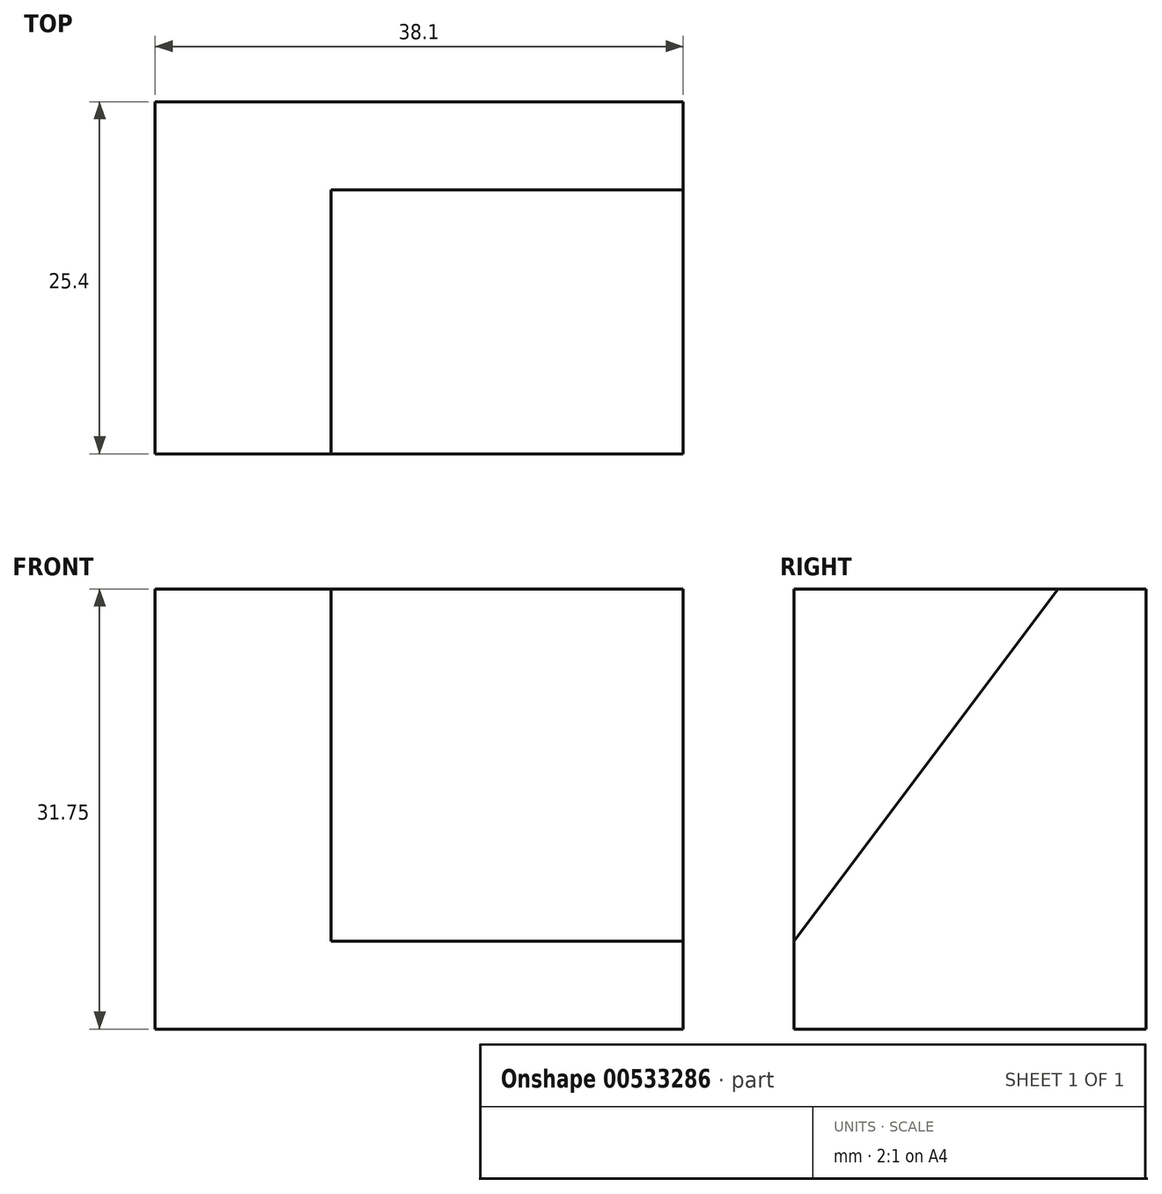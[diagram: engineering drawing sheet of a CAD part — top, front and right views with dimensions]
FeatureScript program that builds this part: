
annotation { "Feature Type Name" : "Feature", "Feature Type Description" : "" }
export const myFeature = defineFeature(function(context is Context, id is Id, definition is map)
    precondition{}
    {
        {
            var Q0;
            Q0=qCreatedBy(makeId("Front.planeOp"),FACE);
            var sketch = newSketch(context, id + "F0", { "sketchPlane" : qUnion([Q0])});
            skLineSegment(sketch, "E0", {"start": v(-59.7, 0) * mm, "end": v(-21.6, 0) * mm});
            skLineSegment(sketch, "E1", {"start": v(-59.7, 0) * mm, "end": v(-59.7, 31.75) * mm});
            skLineSegment(sketch, "E2", {"start": v(-21.6, 0) * mm, "end": v(-21.6, 31.75) * mm});
            skLineSegment(sketch, "E3", {"start": v(-21.6, 31.75) * mm, "end": v(-59.7, 31.75) * mm});
            skSolve(sketch);
        }
        {
            var Q0;
            Q0=makeQuery(id+"F0.imprint","IMPRINT",FACE,{"disambiguationData":[TD([[makeQuery(id+"F0.imprint","IMPRINT",EDGE,{"derivedFrom":sQuery(id+"F0.wireOp",EDGE,"E0")}),1.0]])]});
            extrude(context, id + "F1", {"entities" : qUnion([Q0]), "depth" : 25.4 * mm, "offsetDistance" : 25.4 * mm});
        }
        {
            var Q0;
            Q0=makeQuery(id+"F1.opExtrude","CAP_FACE",FACE,{"disambiguationData":[OSD([sQuery(id+"F0.wireOp",EDGE,"E0"),sQuery(id+"F0.wireOp",EDGE,"E1"),sQuery(id+"F0.wireOp",EDGE,"E2"),sQuery(id+"F0.wireOp",EDGE,"E3")])],"isStart":false});
            var sketch = newSketch(context, id + "F2", { "sketchPlane" : qUnion([Q0])});
            skSolve(sketch);
        }
        {
            var Q0;
            Q0=makeQuery(id+"F2.imprint","IMPRINT",FACE,{"disambiguationData":[TD([[makeQuery(id+"F2.imprint","IMPRINT",EDGE,{"derivedFrom":makeQuery(id+"F1.opExtrude","CAP_EDGE",EDGE,{"disambiguationData":[OSD([sQuery(id+"F0.wireOp",EDGE,"E0")])],"isStart":false})}),1.0]])]});
            extrude(context, id + "F3", {"entities" : qUnion([Q0]), "operationType" : NewBodyOperationType.REMOVE, "depth" : 25.4 * mm, "offsetDistance" : 25.4 * mm});
        }
        {
            var Q0;
            Q0=makeQuery(id+"F1.opExtrude","SWEPT_FACE",FACE,{"disambiguationData":[OSD([sQuery(id+"F0.wireOp",EDGE,"E2")])]});
            var sketch = newSketch(context, id + "F4", { "sketchPlane" : qUnion([Q0])});
            skLineSegment(sketch, "E4", {"start": v(-6.35, 31.75) * mm, "end": v(-25.4, 6.35) * mm});
            skSolve(sketch);
        }
        {
            var Q0;
            {var subQ0=sQuery(id+"F4.wireOp",EDGE,"E4");Q0=makeQuery(id+"F4.imprint","IMPRINT",FACE,{"disambiguationData":[TD([[makeQuery(id+"F4.imprint","IMPRINT",EDGE,{"derivedFrom":subQ0}),-1.0]])]});}
            extrude(context, id + "F5", {"entities" : qUnion([Q0]), "operationType" : NewBodyOperationType.REMOVE, "oppositeDirection" : true, "depth" : 25.4 * mm, "offsetDistance" : 25.4 * mm});
        }
    });
